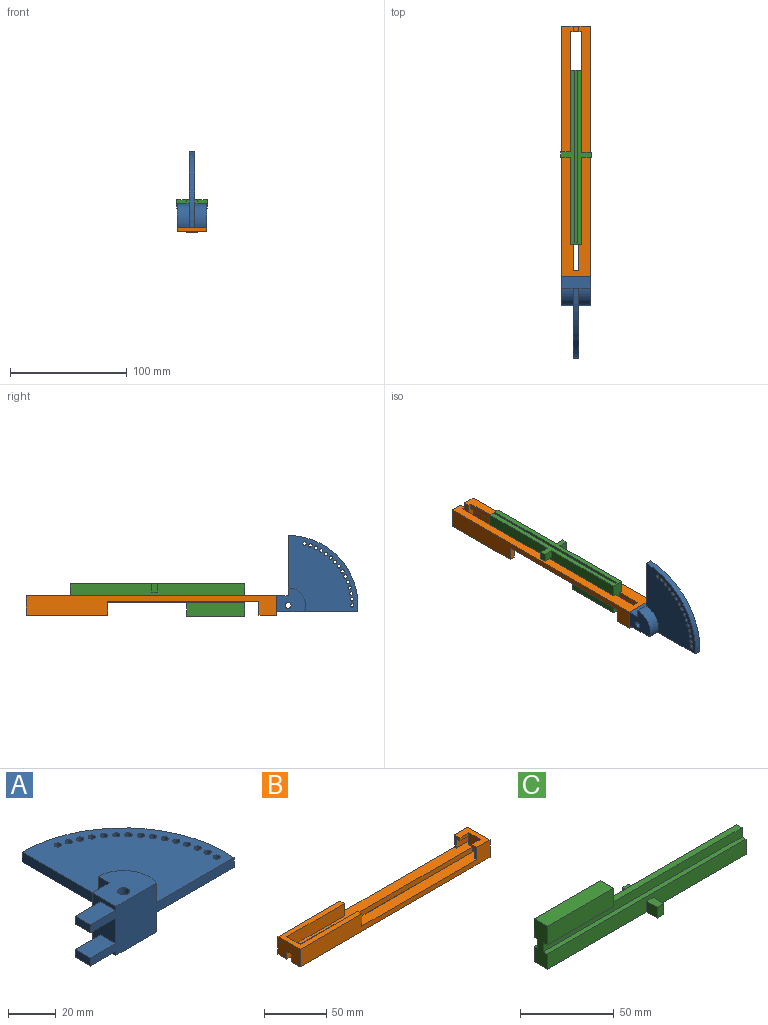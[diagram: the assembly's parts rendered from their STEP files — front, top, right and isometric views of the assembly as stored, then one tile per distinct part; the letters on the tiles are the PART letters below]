
ASSEMBLY  parts=3 mates=4
PART A: 35 faces, bbox 85x65.5x25 mm
  f0: plane 51.5x25mm, normal (-1,0,0), area 387.5mm2, adj f16,f17,f18,f22,f31,f32,f33,f34
  f1: cylinder r=1.5mm len=5mm, axis (0,0,-1), area 47.1mm2, adj f32,f34
  f2: cylinder r=1.5mm len=5mm, axis (0,0,-1), area 47.1mm2, adj f32,f34
  f3: cylinder r=1.5mm len=5mm, axis (0,0,-1), area 47.1mm2, adj f32,f34
  f4: cylinder r=1.5mm len=5mm, axis (0,0,-1), area 47.1mm2, adj f32,f34
  f5: cylinder r=1.5mm len=5mm, axis (0,0,-1), area 47.1mm2, adj f32,f34
  f6: cylinder r=1.5mm len=5mm, axis (0,0,-1), area 47.1mm2, adj f32,f34
  f7: cylinder r=1.5mm len=5mm, axis (0,0,-1), area 47.1mm2, adj f32,f34
  f8: cylinder r=1.5mm len=5mm, axis (0,0,-1), area 47.1mm2, adj f32,f34
  f9: cylinder r=1.5mm len=5mm, axis (0,0,-1), area 47.1mm2, adj f32,f34
  f10: cylinder r=1.5mm len=5mm, axis (0,0,-1), area 47.1mm2, adj f32,f34
  f11: cylinder r=1.5mm len=5mm, axis (0,0,-1), area 47.1mm2, adj f32,f34
  f12: cylinder r=1.5mm len=5mm, axis (0,0,-1), area 47.1mm2, adj f32,f34
  f13: cylinder r=1.5mm len=5mm, axis (0,0,-1), area 47.1mm2, adj f32,f34
  f14: cylinder r=1.5mm len=5mm, axis (0,0,-1), area 47.1mm2, adj f32,f34
  f15: cylinder r=1.5mm len=5mm, axis (0,0,-1), area 47.1mm2, adj f32,f34
  f16: cylinder r=60mm len=65.5mm, axis (0,0,-1), area 498.8mm2, adj f0,f20,f32,f34
  f17: plane 25x20.5mm, normal (0,0,1), area 377.7mm2, adj f0,f18,f19,f20,f21,f31
  f18: plane 25x10mm, normal (0,1,0), area 250mm2, adj f0,f17,f19,f22
  f19: plane 25x14mm, normal (-1,0,0), area 278mm2, adj f17,f18,f20,f22,f23,f24,f25,f27
  f20: plane 84.75x25mm, normal (0,-1,0), area 947.8mm2, adj f16,f17,f19,f22,f23,f25,f26,f27
  f21: cylinder r=2.5mm len=25mm, axis (0,0,-1), area 392.7mm2, adj f17,f22
  f22: plane 25x20.5mm, normal (0,0,-1), area 377.7mm2, adj f0,f18,f19,f20,f21,f33
  f23: plane 15x9mm, normal (0,0,1), area 135mm2, adj f19,f20,f24,f26
  f24: plane 15x4mm, normal (0,1,0), area 60mm2, adj f19,f23,f25,f26
  f25: plane 15x9mm, normal (0,0,-1), area 135mm2, adj f19,f20,f24,f26
  f26: plane 9x4mm, normal (-1,0,0), area 36mm2, adj f20,f23,f24,f25
  f27: plane 15x9mm, normal (0,0,1), area 135mm2, adj f19,f20,f28,f30
  f28: plane 15x4mm, normal (0,1,0), area 60mm2, adj f19,f27,f29,f30
  f29: plane 15x9mm, normal (0,0,-1), area 135mm2, adj f19,f20,f28,f30
  f30: plane 9x4mm, normal (-1,0,0), area 36mm2, adj f20,f27,f28,f29
  f31: cylinder r=15mm len=20.5mm, axis (0,0,1), area 291.9mm2, adj f0,f17,f20,f32
  f32: plane 65.5x60mm, normal (0,0,1), area 2793.6mm2, adj f0,f1,f2,f3,f4,f5,f6,f7
  f33: cylinder r=15mm len=20.5mm, axis (0,0,-1), area 291.9mm2, adj f0,f20,f22,f34
  f34: plane 65.5x60mm, normal (0,0,-1), area 2793.6mm2, adj f0,f1,f2,f3,f4,f5,f6,f7
PART B: 34 faces, bbox 215x25x17 mm
  f0: plane 10x3mm, normal (0,-1,0), area 30mm2, adj f3,f13,f27,f29
  f1: plane 25x17mm, normal (1,0,0), area 353mm2, adj f4,f5,f6,f18,f19,f27,f28,f29
  f2: plane 12x6mm, normal (-1,0,0), area 36mm2, adj f4,f18,f26,f27,f31,f33
  f3: plane 12x6mm, normal (-1,0,0), area 36mm2, adj f0,f5,f6,f27,f29,f30
  f4: plane 210x10mm, normal (0,0,1), area 1600mm2, adj f1,f2,f9,f13,f14,f15,f16,f18
  f5: plane 210x10mm, normal (0,0,1), area 1600mm2, adj f1,f3,f6,f9,f10,f11,f12,f13
  f6: plane 215x17mm, normal (0,1,0), area 2095mm2, adj f1,f3,f5,f7,f19,f23,f24,f27
  f7: plane 25x17mm, normal (-1,0,0), area 387.5mm2, adj f6,f8,f17,f18,f19,f24,f25
  f8: plane 7.5x5mm, normal (0,-1,0), area 37.5mm2, adj f7,f9,f19,f25
  f9: plane 17x15mm, normal (1,0,0), area 192.5mm2, adj f4,f5,f8,f10,f16,f17,f19,f21
  f10: plane 50x5mm, normal (0,-1,0), area 250mm2, adj f5,f9,f11,f19
  f11: plane 5x2.5mm, normal (-1,0,0), area 12.5mm2, adj f5,f10,f12,f19
  f12: plane 155x5mm, normal (0,-1,0), area 775mm2, adj f5,f11,f13,f19
  f13: plane 17x13mm, normal (-1,0,0), area 181mm2, adj f0,f4,f5,f12,f14,f19,f26,f27
  f14: plane 155x5mm, normal (0,1,0), area 775mm2, adj f4,f13,f15,f19
  f15: plane 5x2.5mm, normal (-1,0,0), area 12.5mm2, adj f4,f14,f16,f19
  f16: plane 50x5mm, normal (0,1,0), area 250mm2, adj f4,f9,f15,f19
  f17: plane 7.5x5mm, normal (0,1,0), area 37.5mm2, adj f7,f9,f19,f25
  f18: plane 215x17mm, normal (0,-1,0), area 2095mm2, adj f1,f2,f4,f7,f19,f20,f24,f27
  f19: plane 215x25mm, normal (0,0,-1), area 4075mm2, adj f1,f6,f7,f8,f9,f10,f11,f12
  f20: plane 12x5mm, normal (1,0,0), area 60mm2, adj f4,f18,f21,f24
  f21: plane 65x12mm, normal (0,1,0), area 780mm2, adj f4,f9,f20,f24
  f22: plane 65x12mm, normal (0,-1,0), area 780mm2, adj f5,f9,f23,f24
  f23: plane 12x5mm, normal (1,0,0), area 60mm2, adj f5,f6,f22,f24
  f24: plane 70x25mm, normal (0,0,1), area 775mm2, adj f6,f7,f9,f18,f20,f21,f22,f23
  f25: plane 5x5mm, normal (0,0,-1), area 25mm2, adj f7,f8,f9,f17
  f26: plane 10x3mm, normal (0,1,0), area 30mm2, adj f2,f13,f27,f33
  f27: plane 25x15mm, normal (0,0,1), area 245mm2, adj f0,f1,f2,f3,f6,f13,f18,f26
  f28: plane 9x5mm, normal (0,1,0), area 45mm2, adj f1,f5,f13,f29
  f29: plane 15x4mm, normal (0,0,-1), area 60mm2, adj f0,f1,f3,f28,f30
  f30: plane 15x9mm, normal (0,-1,0), area 135mm2, adj f1,f3,f5,f29
  f31: plane 15x9mm, normal (0,1,0), area 135mm2, adj f1,f2,f4,f33
  f32: plane 9x5mm, normal (0,-1,0), area 45mm2, adj f1,f4,f13,f33
  f33: plane 15x4mm, normal (0,0,-1), area 60mm2, adj f1,f2,f26,f31,f32
PART C: 28 faces, bbox 150x26x28 mm
  f0: plane 150x3mm, normal (0,0,1), area 450mm2, adj f10,f14,f15,f20
  f1: plane 8x5mm, normal (0,0,1), area 40mm2, adj f3,f4,f5,f6
  f2: plane 8x4.49mm, normal (0,0,1), area 35.9mm2, adj f11,f12,f13,f14
  f3: plane 8x7mm, normal (-1,0,0), area 56mm2, adj f1,f4,f6,f16
  f4: plane 7x5mm, normal (0,-1,0), area 35mm2, adj f1,f3,f5,f16
  f5: plane 8x7mm, normal (1,0,0), area 56mm2, adj f1,f4,f6,f16
  f6: plane 150x10mm, normal (0,-1,0), area 1465mm2, adj f1,f3,f5,f10,f15,f16,f18
  f7: plane 148x7mm, normal (0,1,0), area 1036mm2, adj f8,f10,f16,f17
  f8: plane 7x2mm, normal (1,0,0), area 14mm2, adj f7,f9,f16,f17
  f9: plane 148x7mm, normal (0,-1,0), area 1036mm2, adj f8,f10,f16,f17
  f10: plane 16x10mm, normal (1,0,0), area 110mm2, adj f0,f6,f7,f9,f14,f16,f17,f18
  f11: plane 8x7mm, normal (1,0,0), area 56mm2, adj f2,f12,f14,f16
  f12: plane 7x4.49mm, normal (0,1,0), area 31.4mm2, adj f2,f11,f13,f16
  f13: plane 8x7mm, normal (-1,0,0), area 56mm2, adj f2,f12,f14,f16
  f14: plane 150x10mm, normal (0,1,0), area 1468.6mm2, adj f0,f2,f10,f11,f13,f15,f16
  f15: plane 28x10mm, normal (-1,0,0), area 244mm2, adj f0,f6,f14,f16,f18,f19,f20,f22
  f16: plane 150x26mm, normal (0,0,-1), area 1279.9mm2, adj f3,f4,f5,f6,f7,f8,f9,f10
  f17: plane 148x2mm, normal (0,0,-1), area 296mm2, adj f7,f8,f9,f10
  f18: plane 150x3mm, normal (0,0,1), area 450mm2, adj f6,f10,f15,f19
  f19: plane 150x6mm, normal (0,-1,0), area 900mm2, adj f10,f15,f18,f21,f22
  f20: plane 150x6mm, normal (0,1,0), area 900mm2, adj f0,f10,f15,f21,f27
  f21: plane 100x4mm, normal (0,0,1), area 400mm2, adj f10,f19,f20,f23
  f22: plane 50x3mm, normal (0,0,-1), area 150mm2, adj f15,f19,f23,f25
  f23: plane 12x10mm, normal (1,0,0), area 120mm2, adj f21,f22,f24,f25,f26,f27
  f24: plane 50x12mm, normal (0,1,0), area 600mm2, adj f15,f23,f26,f27
  f25: plane 50x12mm, normal (0,-1,0), area 600mm2, adj f15,f22,f23,f26
  f26: plane 50x10mm, normal (0,0,1), area 500mm2, adj f15,f23,f24,f25
  f27: plane 50x3mm, normal (0,0,-1), area 150mm2, adj f15,f20,f23,f24
PLACE A rot(axis=(0.58,-0.58,-0.58),120deg) t=(0,-10,8.5)mm
PLACE B rot(axis=(0.71,-0.71,0),180deg) t=(-25,0,17)mm fixed
PLACE C rot(axis=(-0.71,-0.71,0),180deg) t=(-7.52,177.1,27)mm
MATE planar A.f23 <-> B.f30  axis (-1,0,0) through (-23,7.5,7.5)mm
MATE planar A.f24 <-> B.f5  axis (0,0,1) through (-23,7.5,12)mm
MATE planar B.f1 <-> A.f19  axis (0,-1,0) through (-6,0,12)mm
MATE planar B.f19 <-> C.f18  axis (0,0,1) through (-12.5,102.1,17)mm
